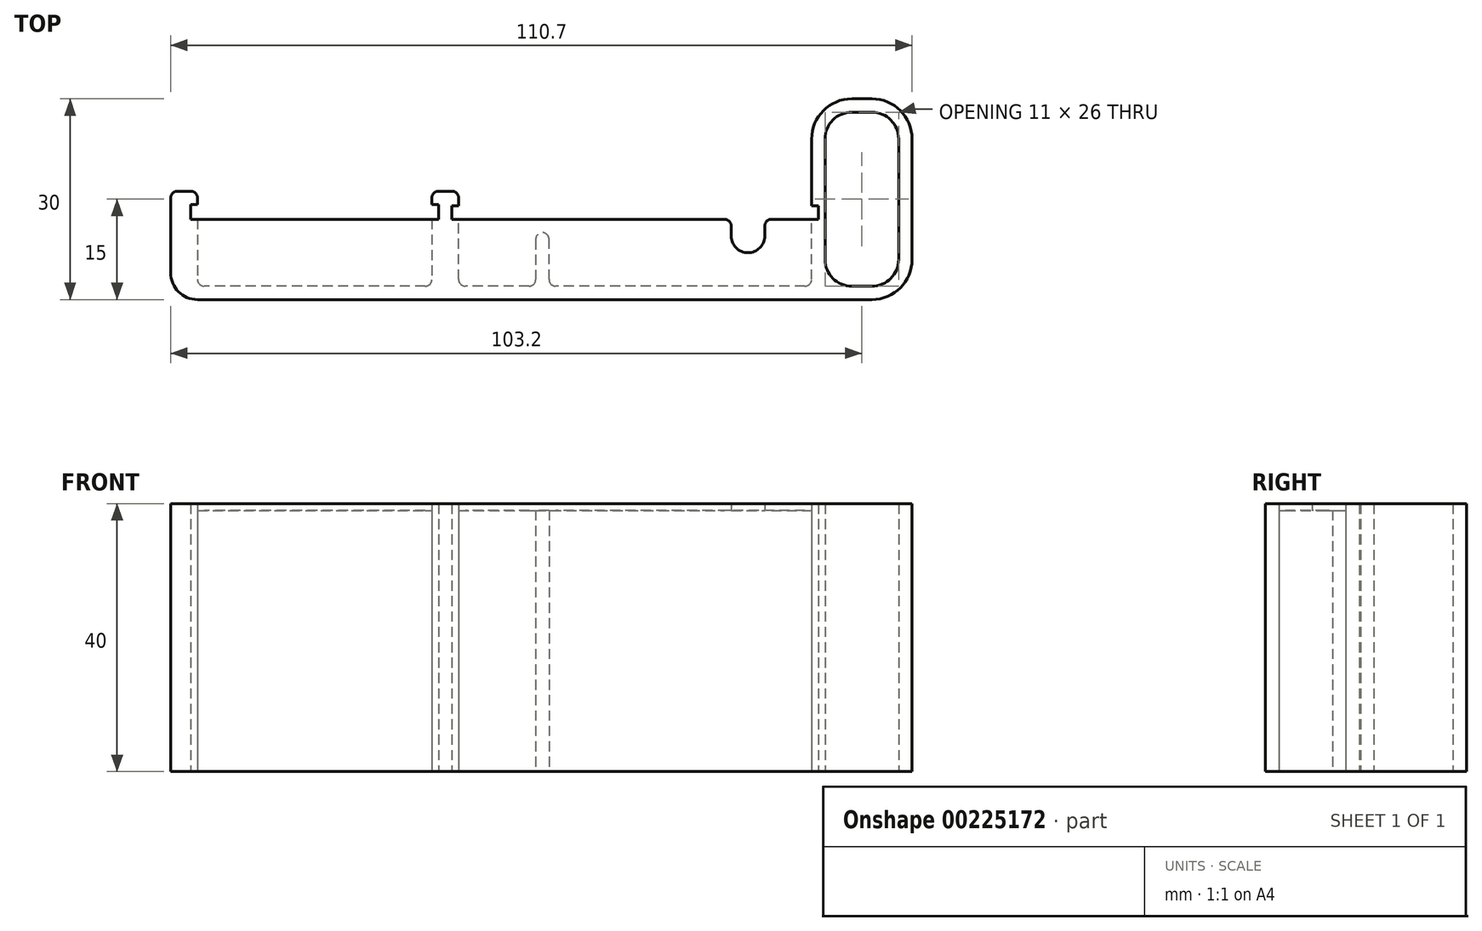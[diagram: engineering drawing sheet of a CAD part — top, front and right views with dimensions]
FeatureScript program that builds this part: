
annotation { "Feature Type Name" : "Feature", "Feature Type Description" : "" }
export const myFeature = defineFeature(function(context is Context, id is Id, definition is map)
    precondition{}
    {
        {
            var Q0;
            Q0=qCreatedBy(makeId("Top.planeOp"),FACE);
            var sketch = newSketch(context, id + "F0", { "sketchPlane" : qUnion([Q0])});
            skLineSegment(sketch, "E0.bottom", {"start": v(55.35, -15) * mm, "end": v(-55.35, -15) * mm});
            skLineSegment(sketch, "E0.top", {"start": v(55.35, 15) * mm, "end": v(-55.35, 15) * mm});
            skLineSegment(sketch, "E0.left", {"start": v(55.35, -15) * mm, "end": v(55.35, 15) * mm});
            skLineSegment(sketch, "E0.right", {"start": v(-55.35, -15) * mm, "end": v(-55.35, 15) * mm});
            skPoint(sketch, "E0.middle", {"position": v(0, 0) * mm});
            skLineSegment(sketch, "E1.bottom", {"start": v(53.35, -13) * mm, "end": v(42.35, -13) * mm});
            skLineSegment(sketch, "E1.top", {"start": v(53.35, 13) * mm, "end": v(42.35, 13) * mm});
            skLineSegment(sketch, "E1.left", {"start": v(53.35, -13) * mm, "end": v(53.35, 13) * mm});
            skLineSegment(sketch, "E1.right", {"start": v(42.35, -13) * mm, "end": v(42.35, 13) * mm});
            skPoint(sketch, "E1.middle", {"position": v(47.85, 0) * mm});
            skLineSegment(sketch, "E2", {"start": v(40.35, -15) * mm, "end": v(40.35, 15) * mm});
            skLineSegment(sketch, "E3", {"start": v(40.35, -13) * mm, "end": v(-55.35, -13) * mm});
            skLineSegment(sketch, "E4", {"start": v(40.35, -3) * mm, "end": v(41.35, -3) * mm});
            skLineSegment(sketch, "E5", {"start": v(41.35, -3) * mm, "end": v(41.35, -1) * mm});
            skLineSegment(sketch, "E6", {"start": v(41.35, -1) * mm, "end": v(40.35, -1) * mm});
            skLineSegment(sketch, "E7", {"start": v(-12.35, -13) * mm, "end": v(-12.35, 15) * mm});
            skLineSegment(sketch, "E8", {"start": v(-12.35, -3) * mm, "end": v(-13.35, -3) * mm});
            skLineSegment(sketch, "E9", {"start": v(-13.35, -3) * mm, "end": v(-13.35, -1) * mm});
            skLineSegment(sketch, "E10", {"start": v(-13.35, -1) * mm, "end": v(-12.35, -1) * mm});
            skLineSegment(sketch, "E11", {"start": v(-16.35, 15) * mm, "end": v(-16.35, -13) * mm});
            skLineSegment(sketch, "E12", {"start": v(-16.35, -3) * mm, "end": v(-15.35, -3) * mm});
            skLineSegment(sketch, "E13", {"start": v(-15.35, -3) * mm, "end": v(-15.35, -0.8) * mm});
            skLineSegment(sketch, "E14", {"start": v(-16.35, -0.8) * mm, "end": v(-15.35, -0.8) * mm});
            skLineSegment(sketch, "E15", {"start": v(-51.35, 15) * mm, "end": v(-51.35, -13) * mm});
            skLineSegment(sketch, "E16", {"start": v(-51.35, -3) * mm, "end": v(-52.35, -3) * mm});
            skLineSegment(sketch, "E17", {"start": v(-52.35, -3) * mm, "end": v(-52.35, -0.8) * mm});
            skLineSegment(sketch, "E18", {"start": v(-52.35, -0.8) * mm, "end": v(-51.35, -0.8) * mm});
            skLineSegment(sketch, "E19", {"start": v(-51.35, 1.2) * mm, "end": v(-55.35, 1.2) * mm});
            skLineSegment(sketch, "E20", {"start": v(-16.35, 1.2) * mm, "end": v(-12.35, 1.2) * mm});
            skLineSegment(sketch, "E21", {"start": v(40.35, 1.2) * mm, "end": v(42.35, 1.2) * mm});
            skLineSegment(sketch, "E22", {"start": v(40.35, 1.2) * mm, "end": v(40.35, 15) * mm});
            skLineSegment(sketch, "E23", {"start": v(1.15, -13) * mm, "end": v(1.15, -5) * mm});
            skLineSegment(sketch, "E24", {"start": v(1.15, -5) * mm, "end": v(-0.85, -5) * mm});
            skLineSegment(sketch, "E25", {"start": v(-0.85, -5) * mm, "end": v(-0.85, -13) * mm});
            skLineSegment(sketch, "E26", {"start": v(-51.35, -3) * mm, "end": v(-16.35, -3) * mm});
            skLineSegment(sketch, "E27", {"start": v(-12.35, -3) * mm, "end": v(40.35, -3) * mm});
            skCircle(sketch, "E28", {"center": v(30.85, -5.5) * mm, "radius": 2.5 * mm});
            skLineSegment(sketch, "E29", {"start": v(28.35, -5.5) * mm, "end": v(28.35, -3) * mm});
            skLineSegment(sketch, "E30", {"start": v(33.35, -5.5) * mm, "end": v(33.35, -3) * mm});
            skSolve(sketch);
        }
        {
            var Q0;
            {var subQ9=sQuery(id+"F0.wireOp",EDGE,"E0.left");Q0=makeQuery(id+"F0.imprint","IMPRINT",FACE,{"disambiguationData":[TD([[makeQuery(id+"F0.imprint","IMPRINT",EDGE,{"derivedFrom":subQ9}),1.0]])]});}
            var Q1;
            {var subQ4=sQuery(id+"F0.wireOp",EDGE,"E0.bottom");var subQ6=sQuery(id+"F0.wireOp",EDGE,"E0.right");var subQ7=makeQuery(id+"F0.imprint","INTERSECT",VERTEX,{"derivedFrom":[subQ4,subQ6]});Q1=makeQuery(id+"F0.imprint","IMPRINT",FACE,{"disambiguationData":[TD([[makeQuery(id+"F0.imprint","IMPRINT",EDGE,{"disambiguationData":[TD([[subQ7,1.0]])],"derivedFrom":subQ4}),-1.0]])]});}
            var Q2;
            {var subQ9=sQuery(id+"F0.wireOp",EDGE,"E8");Q2=makeQuery(id+"F0.imprint","IMPRINT",FACE,{"disambiguationData":[TD([[makeQuery(id+"F0.imprint","IMPRINT",EDGE,{"derivedFrom":subQ9}),1.0]])]});}
            var Q3;
            {var subQ3=sQuery(id+"F0.wireOp",EDGE,"E16");Q3=makeQuery(id+"F0.imprint","IMPRINT",FACE,{"disambiguationData":[TD([[makeQuery(id+"F0.imprint","IMPRINT",EDGE,{"derivedFrom":subQ3}),1.0]])]});}
            var Q4;
            {var subQ0=sQuery(id+"F0.wireOp",EDGE,"E23");Q4=makeQuery(id+"F0.imprint","IMPRINT",FACE,{"disambiguationData":[TD([[makeQuery(id+"F0.imprint","IMPRINT",EDGE,{"derivedFrom":subQ0}),1.0]])]});}
            var Q5;
            {var subQ5=sQuery(id+"F0.wireOp",EDGE,"E26");Q5=makeQuery(id+"F0.imprint","IMPRINT",FACE,{"disambiguationData":[TD([[makeQuery(id+"F0.imprint","IMPRINT",EDGE,{"derivedFrom":subQ5}),-1.0]])]});}
            var Q6;
            {var subQ7=sQuery(id+"F0.wireOp",EDGE,"E23");Q6=makeQuery(id+"F0.imprint","IMPRINT",FACE,{"disambiguationData":[TD([[makeQuery(id+"F0.imprint","IMPRINT",EDGE,{"derivedFrom":subQ7}),-1.0]])]});}
            extrude(context, id + "F1", {"entities" : qUnion([Q0, Q1, Q2, Q3, Q4, Q5, Q6]), "depth" : 40 * mm});
        }
        {
            var Q0;
            {var subQ5=sQuery(id+"F0.wireOp",EDGE,"E26");Q0=makeQuery(id+"F0.imprint","IMPRINT",FACE,{"disambiguationData":[TD([[makeQuery(id+"F0.imprint","IMPRINT",EDGE,{"derivedFrom":subQ5}),-1.0]])]});}
            var Q1;
            {var subQ7=sQuery(id+"F0.wireOp",EDGE,"E23");Q1=makeQuery(id+"F0.imprint","IMPRINT",FACE,{"disambiguationData":[TD([[makeQuery(id+"F0.imprint","IMPRINT",EDGE,{"derivedFrom":subQ7}),-1.0]])]});}
            extrude(context, id + "F2", {"entities" : qUnion([Q0, Q1]), "operationType" : NewBodyOperationType.REMOVE, "depth" : 39 * mm});
        }
        {
            var Q0;
            Q0=makeQuery(id+"F1.opExtrude","SWEPT_EDGE",EDGE,{"disambiguationData":[OSD([sQuery(id+"F0.wireOp",EDGE,"E1.bottom"),sQuery(id+"F0.wireOp",EDGE,"E1.right")])]});
            var Q1;
            Q1=makeQuery(id+"F1.opExtrude","SWEPT_EDGE",EDGE,{"disambiguationData":[OSD([sQuery(id+"F0.wireOp",EDGE,"E1.bottom"),sQuery(id+"F0.wireOp",EDGE,"E1.left")])]});
            var Q2;
            Q2=makeQuery(id+"F1.opExtrude","SWEPT_EDGE",EDGE,{"disambiguationData":[OSD([sQuery(id+"F0.wireOp",EDGE,"E1.top"),sQuery(id+"F0.wireOp",EDGE,"E1.left")])]});
            var Q3;
            Q3=makeQuery(id+"F1.opExtrude","SWEPT_EDGE",EDGE,{"disambiguationData":[OSD([sQuery(id+"F0.wireOp",EDGE,"E1.top"),sQuery(id+"F0.wireOp",EDGE,"E1.right")])]});
            var Q4;
            Q4=makeQuery(id+"F1.opExtrude","SWEPT_EDGE",EDGE,{"disambiguationData":[OSD([sQuery(id+"F0.wireOp",EDGE,"E0.bottom"),sQuery(id+"F0.wireOp",EDGE,"E0.right")])]});
            fillet(context, id + "F3", {"entities" : qUnion([Q0, Q1, Q2, Q3, Q4]), "radius" : 4 * mm, "tangentPropagation" : true, "allowEdgeOverflow" : false});
        }
        {
            var Q0;
            Q0=makeQuery(id+"F2.boolean.opBoolean","COPY",EDGE,{"derivedFrom":makeQuery(id+"F2.opExtrude","SWEPT_EDGE",EDGE,{"disambiguationData":[OSD([sQuery(id+"F0.wireOp",EDGE,"E2"),sQuery(id+"F0.wireOp",EDGE,"E3")])]})});
            var Q1;
            Q1=makeQuery(id+"F2.boolean.opBoolean","COPY",EDGE,{"derivedFrom":makeQuery(id+"F2.opExtrude","SWEPT_EDGE",EDGE,{"disambiguationData":[OSD([sQuery(id+"F0.wireOp",EDGE,"E3"),sQuery(id+"F0.wireOp",EDGE,"E25")])]})});
            var Q2;
            Q2=makeQuery(id+"F2.boolean.opBoolean","COPY",EDGE,{"derivedFrom":makeQuery(id+"F2.opExtrude","SWEPT_EDGE",EDGE,{"disambiguationData":[OSD([sQuery(id+"F0.wireOp",EDGE,"E24"),sQuery(id+"F0.wireOp",EDGE,"E25")])]})});
            var Q3;
            Q3=makeQuery(id+"F2.boolean.opBoolean","COPY",EDGE,{"derivedFrom":makeQuery(id+"F2.opExtrude","SWEPT_EDGE",EDGE,{"disambiguationData":[OSD([sQuery(id+"F0.wireOp",EDGE,"E3"),sQuery(id+"F0.wireOp",EDGE,"E11")])]})});
            var Q4;
            Q4=makeQuery(id+"F1.opExtrude","SWEPT_EDGE",EDGE,{"disambiguationData":[OSD([sQuery(id+"F0.wireOp",EDGE,"E11"),sQuery(id+"F0.wireOp",EDGE,"E20")])]});
            var Q5;
            Q5=makeQuery(id+"F1.opExtrude","SWEPT_EDGE",EDGE,{"disambiguationData":[OSD([sQuery(id+"F0.wireOp",EDGE,"E7"),sQuery(id+"F0.wireOp",EDGE,"E20")])]});
            var Q6;
            Q6=makeQuery(id+"F1.opExtrude","SWEPT_EDGE",EDGE,{"disambiguationData":[OSD([sQuery(id+"F0.wireOp",EDGE,"E0.right"),sQuery(id+"F0.wireOp",EDGE,"E19")])]});
            var Q7;
            Q7=makeQuery(id+"F1.opExtrude","SWEPT_EDGE",EDGE,{"disambiguationData":[OSD([sQuery(id+"F0.wireOp",EDGE,"E15"),sQuery(id+"F0.wireOp",EDGE,"E19")])]});
            var Q8;
            Q8=makeQuery(id+"F2.boolean.opBoolean","COPY",EDGE,{"derivedFrom":makeQuery(id+"F2.opExtrude","SWEPT_EDGE",EDGE,{"disambiguationData":[OSD([sQuery(id+"F0.wireOp",EDGE,"E3"),sQuery(id+"F0.wireOp",EDGE,"E15")])]})});
            var Q9;
            Q9=makeQuery(id+"F2.boolean.opBoolean","COPY",EDGE,{"derivedFrom":makeQuery(id+"F2.opExtrude","SWEPT_EDGE",EDGE,{"disambiguationData":[OSD([sQuery(id+"F0.wireOp",EDGE,"E23"),sQuery(id+"F0.wireOp",EDGE,"E24")])]})});
            var Q10;
            Q10=makeQuery(id+"F2.boolean.opBoolean","COPY",EDGE,{"derivedFrom":makeQuery(id+"F2.opExtrude","SWEPT_EDGE",EDGE,{"disambiguationData":[OSD([sQuery(id+"F0.wireOp",EDGE,"E3"),sQuery(id+"F0.wireOp",EDGE,"E23")])]})});
            var Q11;
            Q11=makeQuery(id+"F2.boolean.opBoolean","COPY",EDGE,{"derivedFrom":makeQuery(id+"F2.opExtrude","SWEPT_EDGE",EDGE,{"disambiguationData":[OSD([sQuery(id+"F0.wireOp",EDGE,"E3"),sQuery(id+"F0.wireOp",EDGE,"E7")])]})});
            var Q12;
            Q12=makeQuery(id+"F1.opExtrude","SWEPT_EDGE",EDGE,{"disambiguationData":[OSD([sQuery(id+"F0.wireOp",EDGE,"E27"),sQuery(id+"F0.wireOp",EDGE,"E30")])]});
            var Q13;
            Q13=makeQuery(id+"F1.opExtrude","SWEPT_EDGE",EDGE,{"disambiguationData":[OSD([sQuery(id+"F0.wireOp",EDGE,"E27"),sQuery(id+"F0.wireOp",EDGE,"E29")])]});
            fillet(context, id + "F4", {"entities" : qUnion([Q0, Q1, Q2, Q3, Q4, Q5, Q6, Q7, Q8, Q9, Q10, Q11, Q12, Q13]), "radius" : 1 * mm, "tangentPropagation" : true, "allowEdgeOverflow" : false});
        }
        {
            var Q0;
            Q0=makeQuery(id+"F1.opExtrude","SWEPT_EDGE",EDGE,{"disambiguationData":[OSD([sQuery(id+"F0.wireOp",EDGE,"E0.top"),sQuery(id+"F0.wireOp",EDGE,"E22")])]});
            var Q1;
            Q1=makeQuery(id+"F1.opExtrude","SWEPT_EDGE",EDGE,{"disambiguationData":[OSD([sQuery(id+"F0.wireOp",EDGE,"E0.top"),sQuery(id+"F0.wireOp",EDGE,"E0.left")])]});
            var Q2;
            Q2=makeQuery(id+"F1.opExtrude","SWEPT_EDGE",EDGE,{"disambiguationData":[OSD([sQuery(id+"F0.wireOp",EDGE,"E0.bottom"),sQuery(id+"F0.wireOp",EDGE,"E0.left")])]});
            fillet(context, id + "F5", {"entities" : qUnion([Q0, Q1, Q2]), "radius" : 6 * mm, "tangentPropagation" : true, "allowEdgeOverflow" : false});
        }
    });
